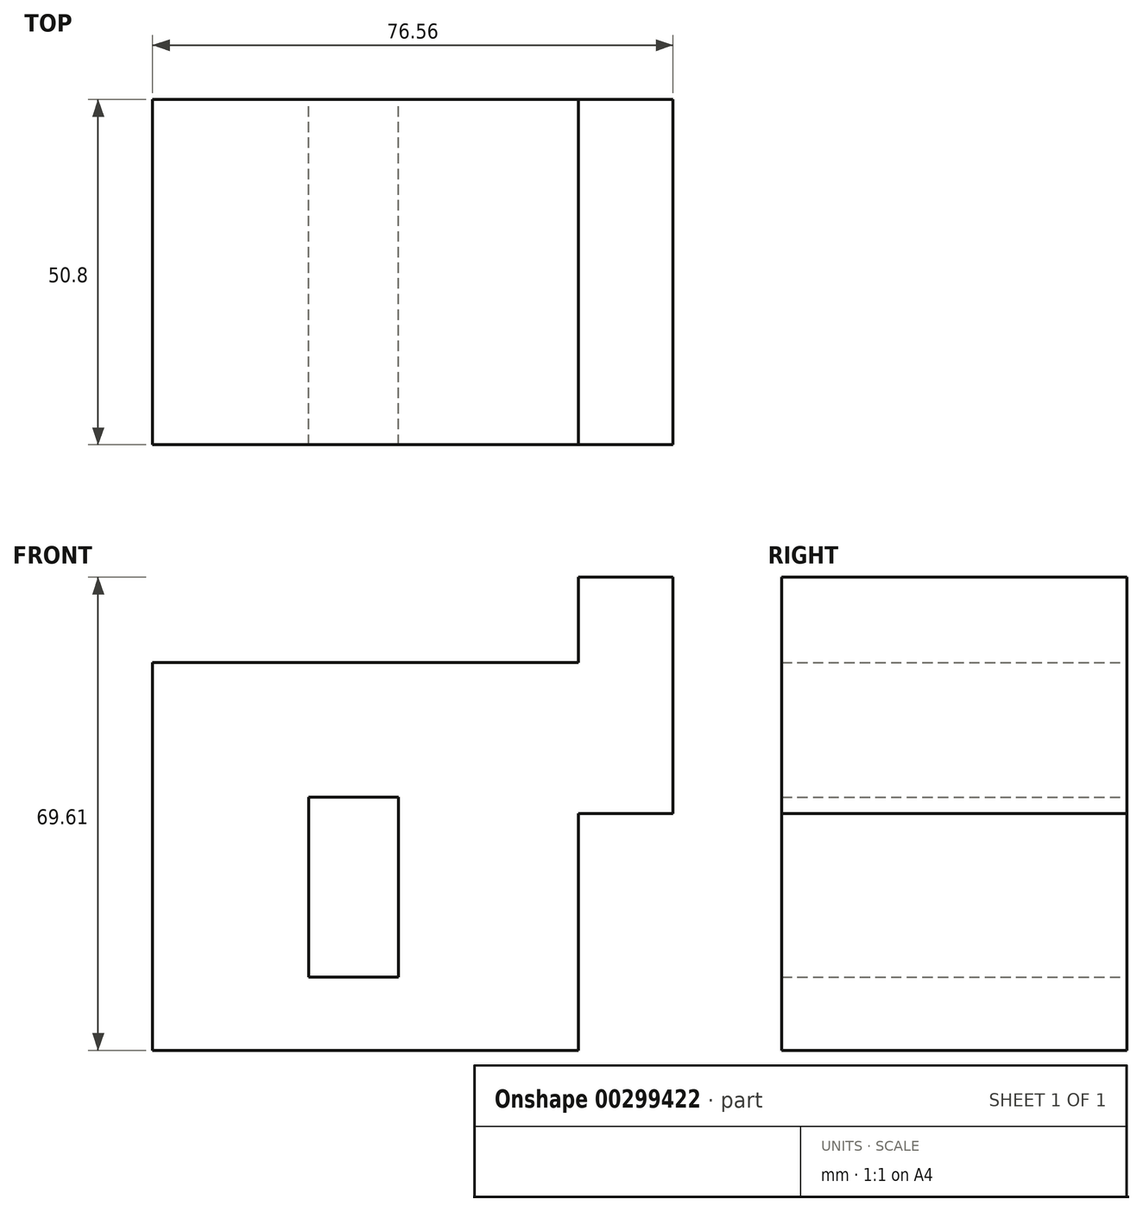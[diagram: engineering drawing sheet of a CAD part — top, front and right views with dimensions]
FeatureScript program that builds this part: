
annotation { "Feature Type Name" : "Feature", "Feature Type Description" : "" }
export const myFeature = defineFeature(function(context is Context, id is Id, definition is map)
    precondition{}
    {
        {
            var Q0;
            Q0=qCreatedBy(makeId("Front.planeOp"),FACE);
            var sketch = newSketch(context, id + "F0", { "sketchPlane" : qUnion([Q0])});
            skLineSegment(sketch, "E0.bottom", {"start": v(19.68, 44.16) * mm, "end": v(33.6, 44.16) * mm});
            skLineSegment(sketch, "E0.top", {"start": v(-42.96, -25.45) * mm, "end": v(19.68, -25.45) * mm});
            skLineSegment(sketch, "E0.left", {"start": v(-42.96, 31.63) * mm, "end": v(-42.96, -25.45) * mm});
            skLineSegment(sketch, "E0.right", {"start": v(33.6, 44.16) * mm, "end": v(33.6, 9.36) * mm});
            skLineSegment(sketch, "E1.bottom", {"start": v(-42.96, 31.63) * mm, "end": v(19.68, 31.63) * mm});
            skLineSegment(sketch, "E1.right", {"start": v(19.68, 31.63) * mm, "end": v(19.68, 44.16) * mm});
            skLineSegment(sketch, "E2.bottom", {"start": v(-20, 11.8) * mm, "end": v(-6.77, 11.8) * mm});
            skLineSegment(sketch, "E2.top", {"start": v(-20, -14.66) * mm, "end": v(-6.77, -14.66) * mm});
            skLineSegment(sketch, "E2.left", {"start": v(-20, 11.8) * mm, "end": v(-20, -14.66) * mm});
            skLineSegment(sketch, "E2.right", {"start": v(-6.77, 11.8) * mm, "end": v(-6.77, -14.66) * mm});
            skLineSegment(sketch, "E3.top", {"start": v(19.68, 9.36) * mm, "end": v(33.6, 9.36) * mm});
            skLineSegment(sketch, "E3.left", {"start": v(19.68, -25.45) * mm, "end": v(19.68, 9.36) * mm});
            skPoint(sketch, "E4.orphan", {"position": v(33.6, -25.45) * mm});
            skSolve(sketch);
        }
        {
            var Q0;
            Q0=makeQuery(id+"F0.imprint","IMPRINT",FACE,{"disambiguationData":[TD([[makeQuery(id+"F0.imprint","IMPRINT",EDGE,{"derivedFrom":sQuery(id+"F0.wireOp",EDGE,"E0.bottom")}),-1.0]])]});
            extrude(context, id + "F1", {"entities" : qUnion([Q0]), "depth" : 50.8 * mm});
        }
    });
